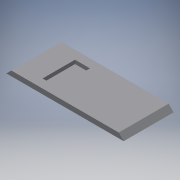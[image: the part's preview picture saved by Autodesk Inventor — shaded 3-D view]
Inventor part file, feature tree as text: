
AUTODESK INVENTOR PART (.ipt)
format: ipt  version: 2018.3 (Build 223284000, 284)  size: 259,072 bytes
history: native  units: mm
features: extrude x4, sketch x4, chamfer x2
ambient origin geometry x8: Origin, YZ Plane, XZ Plane, XY Plane, X Axis, Y Axis, Z Axis, Center Point
bodies: Solid1 (feature_tree)
feature tree (10):
  extrude  "Extrusion1"  Depth=20.0mm
  extrude  "Extrusion2"  Depth=2.0mm
  extrude  "Extrusion3"  Depth=20.0mm TaperAngle=0.0deg
  extrude  "Extrusion4"  Depth=13.0mm
  chamfer  "Chamfer5"  Distance=3.5mm
  chamfer  "Chamfer6"  Distance=3.5mm
  sketch  "Sketch1"  dims[d0=43.0mm d1=20.0mm]
  sketch  "Sketch2"  dims[d2=2.0mm d3=0.0mm d4=2.0mm]
  sketch  "Sketch3"  dims[d5=2.0mm d6=20.0mm d7=0.0mm]
  sketch  "Sketch4"  dims[d8=25.0mm d9=13.0mm d10=3.5mm d11=3.5mm d12=9.0mm d13=9.0mm d14=1.5mm d15=0.0mm d16=19.0mm d17=4.5mm d18=4.5mm d19=1.49mm d20=0.0mm d33=4.5mm d34=1.49mm d35=45.0deg d36=4.5mm d37=1.49mm d38=45.0deg]
